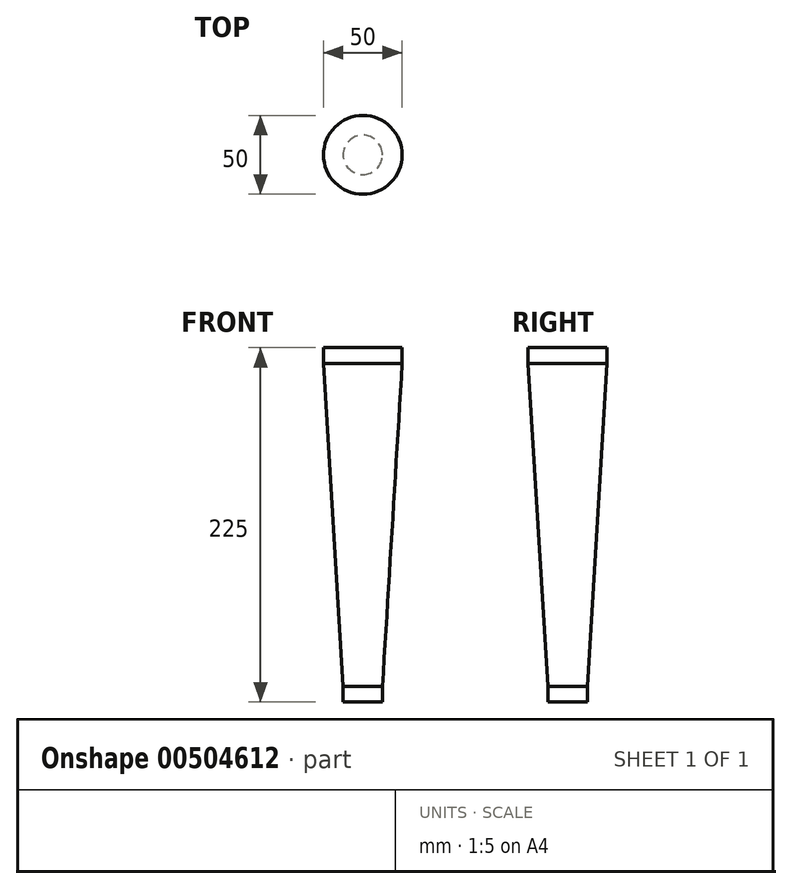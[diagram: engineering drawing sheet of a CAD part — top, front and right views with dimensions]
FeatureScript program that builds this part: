
annotation { "Feature Type Name" : "Feature", "Feature Type Description" : "" }
export const myFeature = defineFeature(function(context is Context, id is Id, definition is map)
    precondition{}
    {
        {
            var Q0;
            Q0=qCreatedBy(makeId("Top.planeOp"),FACE);
            var sketch = newSketch(context, id + "F0", { "sketchPlane" : qUnion([Q0])});
            skCircle(sketch, "E0", {"center": v(0, 0) * mm, "radius": 12.5 * mm});
            skSolve(sketch);
        }
        {
            var Q0;
            Q0=qCreatedBy(makeId("Top.planeOp"),FACE);
            cPlane(context, id + "F1", {"entities" : qUnion([Q0]), "cplaneType" : CPlaneType.OFFSET, "offset" : 205 * mm, "width" : 150 * mm, "height" : 150 * mm});
        }
        {
            var Q0;
            Q0=qCreatedBy(id+"F1.planeOp",FACE);
            var sketch = newSketch(context, id + "F2", { "sketchPlane" : qUnion([Q0])});
            skCircle(sketch, "E1", {"center": v(0, 0) * mm, "radius": 25 * mm});
            skSolve(sketch);
        }
        {
            var Q0;
            Q0 = qSketchRegion(id + "F0", true);
            var Q1;
            Q1 = qSketchRegion(id + "F2", true);
            loft(context, id + "F3", {"sheetProfilesArray" : [{ "sheetProfileEntities" : qUnion([Q0]) }, { "sheetProfileEntities" : qUnion([Q1]) }]});
        }
        {
            var Q0;
            Q0=makeQuery(id+"F3.opLoft","CAP_FACE",FACE,{"disambiguationData":[OSD([makeQuery(id+"F2.imprint","IMPRINT",FACE,{"disambiguationData":[TD([[makeQuery(id+"F2.imprint","IMPRINT",EDGE,{"derivedFrom":sQuery(id+"F2.wireOp",EDGE,"E1")}),1.0]])]})])],"isStart":true});
            extrude(context, id + "F4", {"entities" : qUnion([Q0]), "operationType" : NewBodyOperationType.ADD, "depth" : 10 * mm});
        }
        {
            var Q0;
            Q0=makeQuery(id+"F3.opLoft","CAP_FACE",FACE,{"disambiguationData":[OSD([makeQuery(id+"F0.imprint","IMPRINT",FACE,{"disambiguationData":[TD([[makeQuery(id+"F0.imprint","IMPRINT",EDGE,{"derivedFrom":sQuery(id+"F0.wireOp",EDGE,"E0")}),1.0]])]})])],"isStart":true});
            extrude(context, id + "F5", {"entities" : qUnion([Q0]), "operationType" : NewBodyOperationType.ADD, "depth" : 10 * mm});
        }
    });
